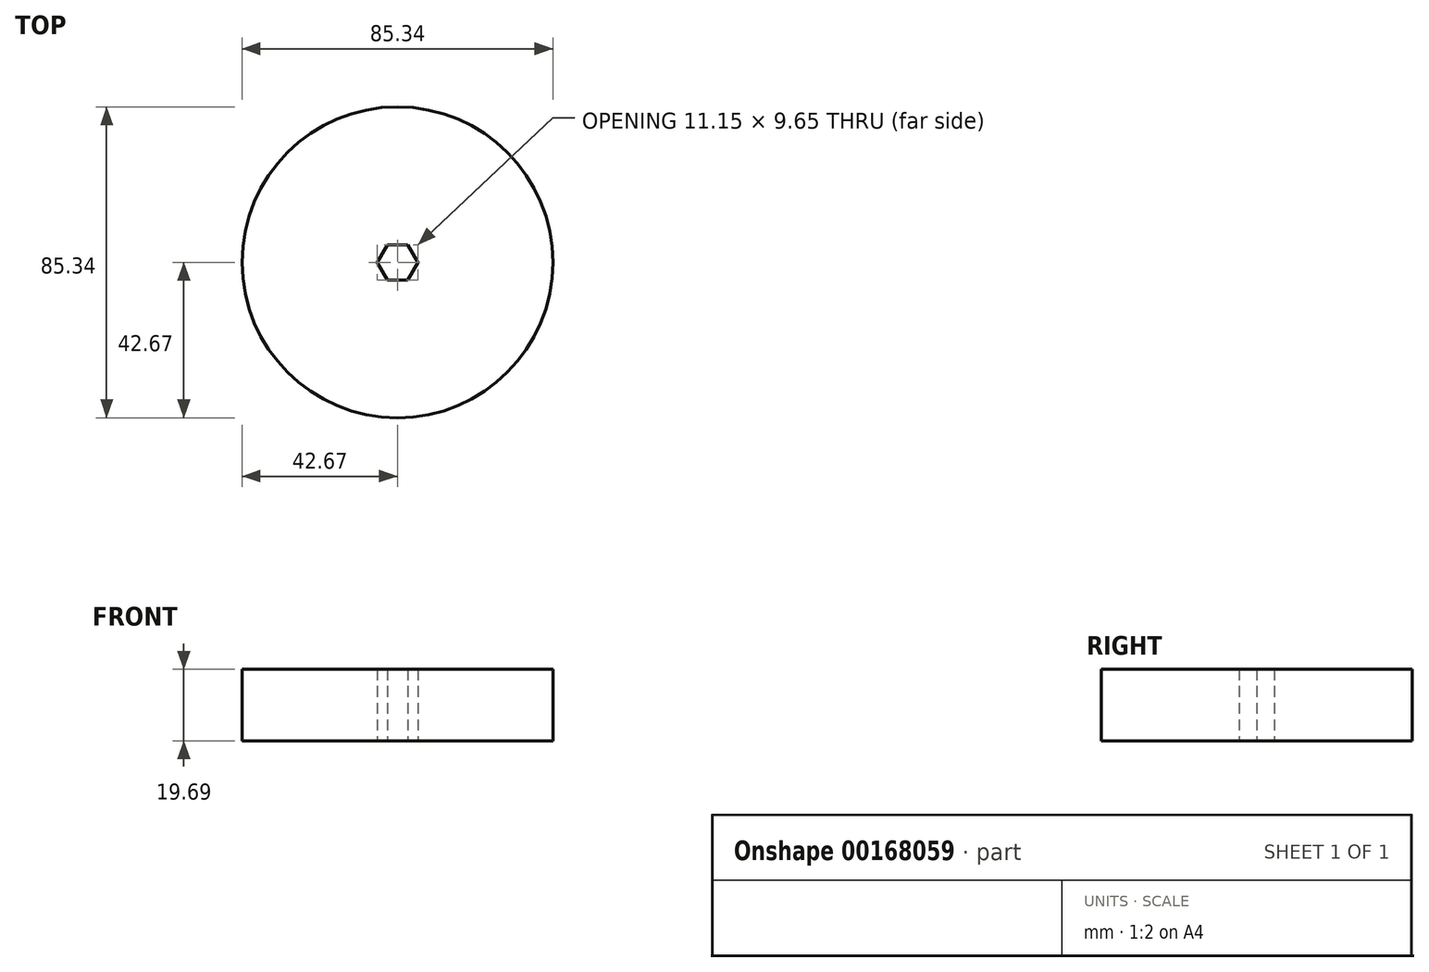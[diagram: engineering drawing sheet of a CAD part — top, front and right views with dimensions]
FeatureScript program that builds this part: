
annotation { "Feature Type Name" : "Feature", "Feature Type Description" : "" }
export const myFeature = defineFeature(function(context is Context, id is Id, definition is map)
    precondition{}
    {
        {
            var Q0;
            Q0=qCreatedBy(makeId("Top.planeOp"),FACE);
            var sketch = newSketch(context, id + "F0", { "sketchPlane" : qUnion([Q0])});
            skCircle(sketch, "E0", {"center": v(0, 0) * mm, "radius": 42.67 * mm});
            skCircle(sketch, "E1.cCircle", {"center": v(0, 0) * mm, "radius": 4.83 * mm, "construction": true});
            skLineSegment(sketch, "E1.0", {"start": v(5.57, 0) * mm, "end": v(2.79, -4.83) * mm});
            skLineSegment(sketch, "E1.1", {"start": v(2.79, -4.83) * mm, "end": v(-2.79, -4.83) * mm});
            skLineSegment(sketch, "E1.2", {"start": v(-2.79, -4.83) * mm, "end": v(-5.57, 0) * mm});
            skLineSegment(sketch, "E1.3", {"start": v(-5.57, 0) * mm, "end": v(-2.79, 4.83) * mm});
            skLineSegment(sketch, "E1.4", {"start": v(-2.79, 4.83) * mm, "end": v(2.79, 4.83) * mm});
            skLineSegment(sketch, "E1.5", {"start": v(2.79, 4.83) * mm, "end": v(5.57, 0) * mm});
            skPoint(sketch, "E1.0.midPoint", {"position": v(4.18, -2.41) * mm});
            skSolve(sketch);
        }
        {
            var Q0;
            Q0=qSketchRegion(id+"F0",true);
            extrude(context, id + "F1", {"entities" : qUnion([Q0]), "depth" : 19.68 * mm});
        }
    });
